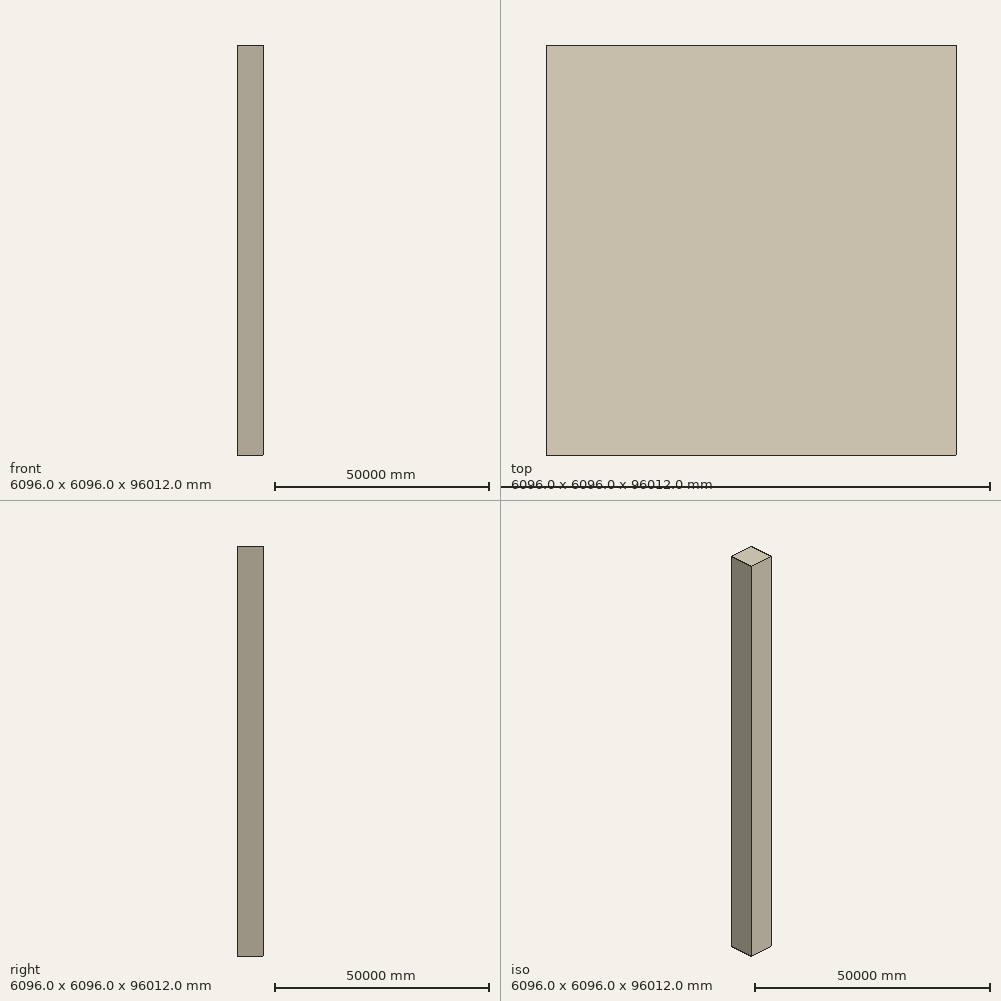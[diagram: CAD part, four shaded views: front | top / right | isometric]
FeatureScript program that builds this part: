
annotation { "Feature Type Name" : "Feature", "Feature Type Description" : "" }
export const myFeature = defineFeature(function(context is Context, id is Id, definition is map)
    precondition{}
    {
        {
            var Q0;
            Q0=qCreatedBy(makeId("Top.planeOp"),FACE);
            var sketch = newSketch(context, id + "F0", { "sketchPlane" : qUnion([Q0])});
            skLineSegment(sketch, "E0", {"start": v(0, 0) * mm, "end": v(6096, 0) * mm});
            skLineSegment(sketch, "E1", {"start": v(6096, 0) * mm, "end": v(6096, 6096) * mm});
            skLineSegment(sketch, "E2", {"start": v(6096, 6096) * mm, "end": v(0, 6096) * mm});
            skLineSegment(sketch, "E3", {"start": v(0, 6096) * mm, "end": v(0, 0) * mm});
            skSolve(sketch);
        }
        {
            var Q0;
            Q0=makeQuery(id+"F0.imprint","IMPRINT",FACE,{"disambiguationData":[TD([[makeQuery(id+"F0.imprint","IMPRINT",EDGE,{"derivedFrom":sQuery(id+"F0.wireOp",EDGE,"E0")}),1.0]])]});
            extrude(context, id + "F1", {"entities" : qUnion([Q0]), "depth" : 96012 * mm, "offsetDistance" : 30.48 * mm});
        }
    });
